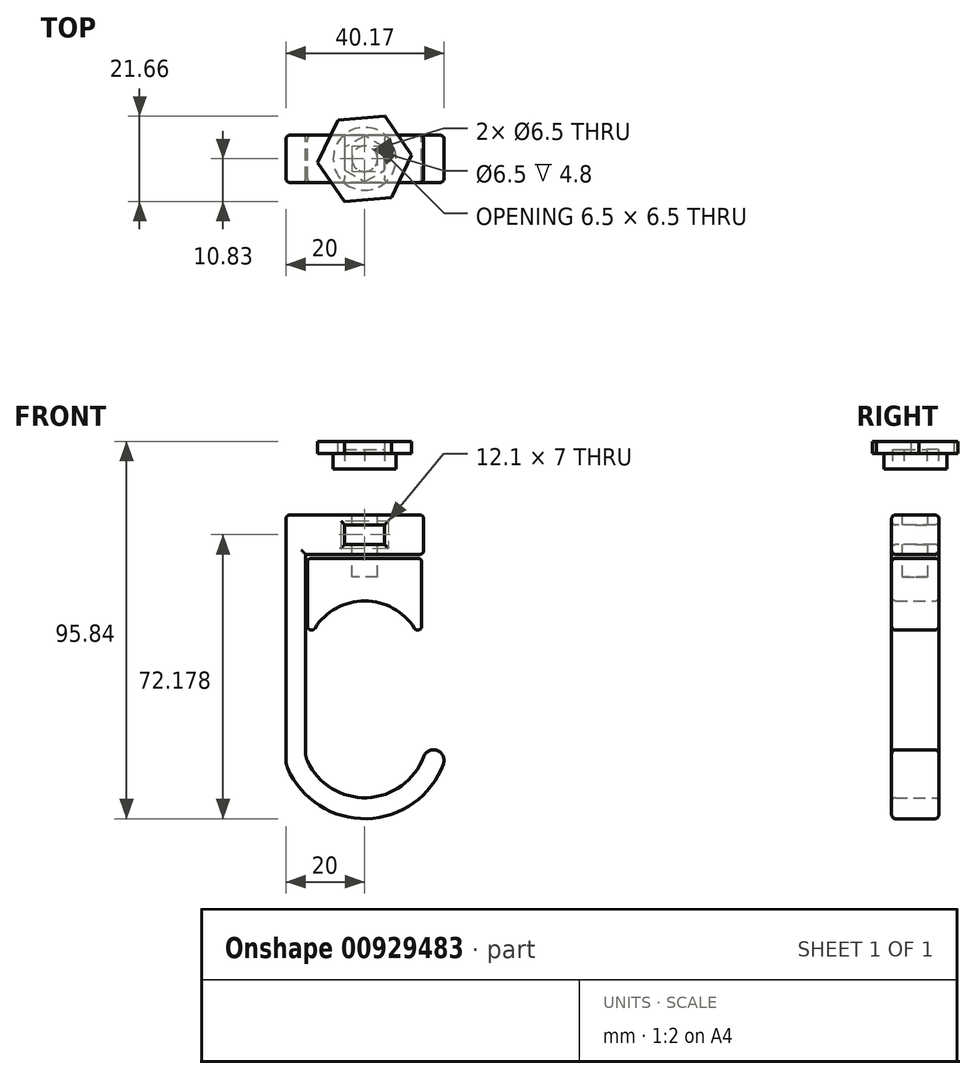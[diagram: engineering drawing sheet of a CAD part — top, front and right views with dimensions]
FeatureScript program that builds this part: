
annotation { "Feature Type Name" : "Feature", "Feature Type Description" : "" }
export const myFeature = defineFeature(function(context is Context, id is Id, definition is map)
    precondition{}
    {
        {
            var Q0;
            Q0=qCreatedBy(makeId("Front.planeOp"),FACE);
            var sketch = newSketch(context, id + "F0", { "sketchPlane" : qUnion([Q0])});
            skLineSegment(sketch, "E0", {"start": v(-15, 51.4) * mm, "end": v(-15, 0.99) * mm});
            skLineSegment(sketch, "E1", {"start": v(-15, 51.4) * mm, "end": v(15, 51.4) * mm});
            skLineSegment(sketch, "E2", {"start": v(15, 51.4) * mm, "end": v(15, 61.4) * mm});
            skLineSegment(sketch, "E3", {"start": v(15, 61.4) * mm, "end": v(-20, 61.4) * mm});
            skLineSegment(sketch, "E4", {"start": v(-20, 61.4) * mm, "end": v(-20, -0.9) * mm});
            skArc(sketch, "E5", {"start": v(20, -1.86) * mm, "mid": v(18.43, 1.57) * mm, "end": v(15, 0) * mm});
            skLineSegment(sketch, "E6", {"start": v(-14.5, 50.4) * mm, "end": v(14.5, 50.4) * mm});
            skLineSegment(sketch, "E7", {"start": v(14.5, 50.4) * mm, "end": v(14.5, 28.4) * mm});
            skLineSegment(sketch, "E8", {"start": v(-14.5, 50.4) * mm, "end": v(-14.5, 28.4) * mm});
            skPoint(sketch, "E9", {"position": v(0, 50.4) * mm});
            skArc(sketch, "E10", {"start": v(14.5, 28.4) * mm, "mid": v(0, 39.57) * mm, "end": v(-14.5, 28.4) * mm});
            skLineSegment(sketch, "E11", {"start": v(0, 80.07) * mm, "end": v(0, 73.07) * mm});
            skLineSegment(sketch, "E12", {"start": v(12, 77.07) * mm, "end": v(12, 80.07) * mm});
            skLineSegment(sketch, "E13", {"start": v(12, 80.07) * mm, "end": v(0, 80.07) * mm});
            skLineSegment(sketch, "E14", {"start": v(0, 73.07) * mm, "end": v(8, 73.07) * mm});
            skLineSegment(sketch, "E15", {"start": v(8, 73.07) * mm, "end": v(8, 77.07) * mm});
            skLineSegment(sketch, "E16", {"start": v(8, 77.07) * mm, "end": v(12, 77.07) * mm});
            skArc(sketch, "E17", {"start": v(-14.55, -1.1) * mm, "mid": v(0.6, -10.42) * mm, "end": v(15, 0) * mm});
            skArc(sketch, "E18", {"start": v(-19.6, -2.87) * mm, "mid": v(0.55, -15.76) * mm, "end": v(20, -1.86) * mm});
            skPoint(sketch, "E19.visualSharp", {"position": v(-20, -1.86) * mm});
            skArc(sketch, "E19.filletArc", {"start": v(-20, -0.9) * mm, "mid": v(-19.9, -1.9) * mm, "end": v(-19.6, -2.87) * mm});
            skLineSegment(sketch, "E20", {"start": v(-14.5, 42.07) * mm, "end": v(14.5, 42.07) * mm, "construction": true});
            skPoint(sketch, "E21.visualSharp", {"position": v(-15, 0) * mm});
            skArc(sketch, "E21.filletArc", {"start": v(-15, 0.99) * mm, "mid": v(-14.89, -0.08) * mm, "end": v(-14.55, -1.1) * mm});
            skSolve(sketch);
        }
        {
            var Q0;
            Q0=makeQuery(id+"F0.imprint","IMPRINT",FACE,{"disambiguationData":[TD([[makeQuery(id+"F0.imprint","IMPRINT",EDGE,{"derivedFrom":sQuery(id+"F0.wireOp",EDGE,"E0")}),-1.0]])]});
            var Q1;
            Q1=makeQuery(id+"F0.imprint","IMPRINT",FACE,{"disambiguationData":[TD([[makeQuery(id+"F0.imprint","IMPRINT",EDGE,{"derivedFrom":sQuery(id+"F0.wireOp",EDGE,"E6")}),-1.0]])]});
            extrude(context, id + "F1", {"entities" : qUnion([Q0, Q1]), "endBound" : BoundingType.SYMMETRIC, "depth" : 12 * mm, "offsetDistance" : 25 * mm});
        }
        {
            var Q0;
            Q0=makeQuery(id+"F0.imprint","IMPRINT",FACE,{"disambiguationData":[TD([[makeQuery(id+"F0.imprint","IMPRINT",EDGE,{"derivedFrom":sQuery(id+"F0.wireOp",EDGE,"E11")}),1.0]])]});
            var Q1;
            Q1=sQuery(id+"F0.wireOp",EDGE,"E11");
            revolve(context, id + "F2", {"surfaceOperationType" : NewSurfaceOperationType.NEW, "entities" : qUnion([Q0]), "axis" : qUnion([Q1]), "revolveType" : RevolveType.FULL});
        }
        {
            var Q0;
            Q0=makeQuery(id+"F1.opExtrude","SWEPT_FACE",FACE,{"disambiguationData":[OSD([sQuery(id+"F0.wireOp",EDGE,"E3")])]});
            var sketch = newSketch(context, id + "F3", { "sketchPlane" : qUnion([Q0])});
            skCircle(sketch, "E22", {"center": v(0, 0) * mm, "radius": 3.25 * mm});
            skSolve(sketch);
        }
        {
            var Q0;
            Q0=makeQuery(id+"F3.imprint","IMPRINT",FACE,{"disambiguationData":[TD([[makeQuery(id+"F3.imprint","IMPRINT",EDGE,{"derivedFrom":sQuery(id+"F3.wireOp",EDGE,"E22")}),1.0]])]});
            extrude(context, id + "F4", {"entities" : qUnion([Q0]), "operationType" : NewBodyOperationType.REMOVE, "surfaceOperationType" : NewSurfaceOperationType.ADD, "oppositeDirection" : true, "depth" : 15.8 * mm, "offsetDistance" : 25 * mm});
        }
        {
            var Q0;
            Q0=makeQuery(id+"F1.opExtrude","CAP_FACE",FACE,{"disambiguationData":[OSD([sQuery(id+"F0.wireOp",EDGE,"E0"),sQuery(id+"F0.wireOp",EDGE,"GksmTGkL-L8Wo-ihQQ-4q2p-oLHmUtR4vZST"),sQuery(id+"F0.wireOp",EDGE,"E1"),sQuery(id+"F0.wireOp",EDGE,"E2"),sQuery(id+"F0.wireOp",EDGE,"E3"),sQuery(id+"F0.wireOp",EDGE,"E4"),sQuery(id+"F0.wireOp",EDGE,"MIt5A5Y3-FBnd-N0LG-dI1h-DyVFCZma1lgl"),sQuery(id+"F0.wireOp",EDGE,"E5")])],"isStart":false});
            var sketch = newSketch(context, id + "F5", { "sketchPlane" : qUnion([Q0])});
            skLineSegment(sketch, "E23.bottom", {"start": v(-5.05, 58.9) * mm, "end": v(5.05, 58.9) * mm});
            skLineSegment(sketch, "E23.top", {"start": v(-5.05, 53.9) * mm, "end": v(5.05, 53.9) * mm});
            skLineSegment(sketch, "E23.left", {"start": v(-5.05, 58.9) * mm, "end": v(-5.05, 53.9) * mm});
            skLineSegment(sketch, "E23.right", {"start": v(5.05, 58.9) * mm, "end": v(5.05, 53.9) * mm});
            skPoint(sketch, "E24", {"position": v(-5.05, 56.4) * mm});
            skPoint(sketch, "E25", {"position": v(0, 58.9) * mm});
            skLineSegment(sketch, "E26", {"start": v(-9.97, 61.4) * mm, "end": v(-9.97, 51.4) * mm, "construction": true});
            skPoint(sketch, "E27", {"position": v(-9.97, 56.4) * mm});
            skSolve(sketch);
        }
        {
            var Q0;
            Q0=makeQuery(id+"F5.imprint","IMPRINT",FACE,{"disambiguationData":[TD([[makeQuery(id+"F5.imprint","IMPRINT",EDGE,{"derivedFrom":sQuery(id+"F5.wireOp",EDGE,"E23.bottom")}),-1.0]])]});
            extrude(context, id + "F6", {"entities" : qUnion([Q0]), "operationType" : NewBodyOperationType.REMOVE, "oppositeDirection" : true, "depth" : 25 * mm, "offsetDistance" : 25 * mm});
        }
        {
            var Q0;
            Q0=makeQuery(id+"F2.opRevolve","SWEPT_FACE",FACE,{"disambiguationData":[OSD([sQuery(id+"F0.wireOp",EDGE,"E14")])]});
            var sketch = newSketch(context, id + "F7", { "sketchPlane" : qUnion([Q0])});
            skCircle(sketch, "E28.cCircle", {"center": v(0, 0) * mm, "radius": 5.05 * mm, "construction": true});
            skLineSegment(sketch, "E28.0", {"start": v(5.05, 2.92) * mm, "end": v(5.05, -2.92) * mm});
            skLineSegment(sketch, "E28.1", {"start": v(5.05, -2.92) * mm, "end": v(0, -5.83) * mm});
            skLineSegment(sketch, "E28.2", {"start": v(0, -5.83) * mm, "end": v(-5.05, -2.92) * mm});
            skLineSegment(sketch, "E28.3", {"start": v(-5.05, -2.92) * mm, "end": v(-5.05, 2.92) * mm});
            skLineSegment(sketch, "E28.4", {"start": v(-5.05, 2.92) * mm, "end": v(0, 5.83) * mm});
            skLineSegment(sketch, "E28.5", {"start": v(0, 5.83) * mm, "end": v(5.05, 2.92) * mm});
            skPoint(sketch, "E28.0.midPoint", {"position": v(5.05, 0) * mm});
            skSolve(sketch);
        }
        {
            var Q0;
            Q0=makeQuery(id+"F7.imprint","IMPRINT",FACE,{"disambiguationData":[TD([[makeQuery(id+"F7.imprint","IMPRINT",EDGE,{"derivedFrom":sQuery(id+"F7.wireOp",EDGE,"E28.0")}),-1.0]])]});
            var Q1;
            Q1=makeQuery(id+"F2.opRevolve","SWEPT_FACE",FACE,{"disambiguationData":[OSD([sQuery(id+"F0.wireOp",EDGE,"E16")])]});
            extrude(context, id + "F8", {"entities" : qUnion([Q0]), "operationType" : NewBodyOperationType.REMOVE, "oppositeDirection" : true, "depth" : 5 * mm, "endBoundEntityFace" : qUnion([Q1]), "offsetDistance" : 25 * mm});
        }
        {
            var Q0;
            Q0=makeQuery(id+"F2.opRevolve","SWEPT_FACE",FACE,{"disambiguationData":[OSD([sQuery(id+"F0.wireOp",EDGE,"E13")])]});
            var sketch = newSketch(context, id + "F9", { "sketchPlane" : qUnion([Q0])});
            skCircle(sketch, "E29.cCircle", {"center": v(0, 0) * mm, "radius": 10.4 * mm, "construction": true});
            skLineSegment(sketch, "E29.0", {"start": v(5.16, 10.83) * mm, "end": v(11.96, 0.95) * mm});
            skLineSegment(sketch, "E29.1", {"start": v(11.96, 0.95) * mm, "end": v(6.8, -9.89) * mm});
            skLineSegment(sketch, "E29.2", {"start": v(6.8, -9.89) * mm, "end": v(-5.16, -10.83) * mm});
            skLineSegment(sketch, "E29.3", {"start": v(-5.16, -10.83) * mm, "end": v(-11.96, -0.95) * mm});
            skLineSegment(sketch, "E29.4", {"start": v(-11.96, -0.95) * mm, "end": v(-6.8, 9.89) * mm});
            skLineSegment(sketch, "E29.5", {"start": v(-6.8, 9.89) * mm, "end": v(5.16, 10.83) * mm});
            skPoint(sketch, "E29.0.midPoint", {"position": v(8.56, 5.89) * mm});
            skSolve(sketch);
        }
        {
            var Q0;
            Q0=makeQuery(id+"F9.imprint","IMPRINT",FACE,{"disambiguationData":[TD([[makeQuery(id+"F9.imprint","IMPRINT",EDGE,{"derivedFrom":sQuery(id+"F9.wireOp",EDGE,"E29.0")}),-1.0]])]});
            extrude(context, id + "F10", {"entities" : qUnion([Q0]), "oppositeDirection" : true, "depth" : 12 * mm, "offsetDistance" : 25 * mm});
        }
        {
            var Q0;
            Q0=makeQuery(id+"F2.opRevolve","SWEPT_BODY",BODY,{"disambiguationData":[OSD([sQuery(id+"F0.wireOp",EDGE,"E11"),sQuery(id+"F0.wireOp",EDGE,"E12"),sQuery(id+"F0.wireOp",EDGE,"E13"),sQuery(id+"F0.wireOp",EDGE,"E14"),sQuery(id+"F0.wireOp",EDGE,"E15"),sQuery(id+"F0.wireOp",EDGE,"E16")])]});
            var Q1;
            Q1=makeQuery(id+"F10.opExtrude","SWEPT_BODY",BODY,{"disambiguationData":[OSD([sQuery(id+"F9.wireOp",EDGE,"E29.0"),sQuery(id+"F9.wireOp",EDGE,"E29.1"),sQuery(id+"F9.wireOp",EDGE,"E29.2"),sQuery(id+"F9.wireOp",EDGE,"E29.3"),sQuery(id+"F9.wireOp",EDGE,"E29.4"),sQuery(id+"F9.wireOp",EDGE,"E29.5")])]});
            booleanBodies(context, id + "F11", {"operationType" : BooleanOperationType.INTERSECTION, "tools" : qUnion([Q0, Q1])});
        }
        {
            var Q0;
            Q0=makeQuery(id+"F1.opExtrude","CAP_FACE",FACE,{"disambiguationData":[OSD([sQuery(id+"F0.wireOp",EDGE,"E0"),sQuery(id+"F0.wireOp",EDGE,"GksmTGkL-L8Wo-ihQQ-4q2p-oLHmUtR4vZST"),sQuery(id+"F0.wireOp",EDGE,"E1"),sQuery(id+"F0.wireOp",EDGE,"E2"),sQuery(id+"F0.wireOp",EDGE,"E3"),sQuery(id+"F0.wireOp",EDGE,"E4"),sQuery(id+"F0.wireOp",EDGE,"MIt5A5Y3-FBnd-N0LG-dI1h-DyVFCZma1lgl"),sQuery(id+"F0.wireOp",EDGE,"E5")])],"isStart":false});
            var Q1;
            Q1=makeQuery(id+"F1.opExtrude","CAP_FACE",FACE,{"disambiguationData":[OSD([sQuery(id+"F0.wireOp",EDGE,"E0"),sQuery(id+"F0.wireOp",EDGE,"GksmTGkL-L8Wo-ihQQ-4q2p-oLHmUtR4vZST"),sQuery(id+"F0.wireOp",EDGE,"E1"),sQuery(id+"F0.wireOp",EDGE,"E2"),sQuery(id+"F0.wireOp",EDGE,"E3"),sQuery(id+"F0.wireOp",EDGE,"E4"),sQuery(id+"F0.wireOp",EDGE,"MIt5A5Y3-FBnd-N0LG-dI1h-DyVFCZma1lgl"),sQuery(id+"F0.wireOp",EDGE,"E5")])],"isStart":true});
            var Q2;
            Q2=makeQuery(id+"F1.opExtrude","SWEPT_FACE",FACE,{"disambiguationData":[OSD([sQuery(id+"F0.wireOp",EDGE,"E2")])]});
            var Q3;
            Q3=makeQuery(id+"F1.opExtrude","SWEPT_FACE",FACE,{"disambiguationData":[OSD([sQuery(id+"F0.wireOp",EDGE,"E4")])]});
            var Q4;
            Q4=makeQuery(id+"F1.opExtrude","CAP_FACE",FACE,{"disambiguationData":[OSD([sQuery(id+"F0.wireOp",EDGE,"E6"),sQuery(id+"F0.wireOp",EDGE,"E7"),sQuery(id+"F0.wireOp",EDGE,"E8"),sQuery(id+"F0.wireOp",EDGE,"E10")])],"isStart":false});
            var Q5;
            Q5=makeQuery(id+"F1.opExtrude","CAP_FACE",FACE,{"disambiguationData":[OSD([sQuery(id+"F0.wireOp",EDGE,"E6"),sQuery(id+"F0.wireOp",EDGE,"E7"),sQuery(id+"F0.wireOp",EDGE,"E8"),sQuery(id+"F0.wireOp",EDGE,"E10")])],"isStart":true});
            var Q6;
            Q6=makeQuery(id+"F1.opExtrude","SWEPT_FACE",FACE,{"disambiguationData":[OSD([sQuery(id+"F0.wireOp",EDGE,"E7")])]});
            var Q7;
            Q7=makeQuery(id+"F1.opExtrude","SWEPT_FACE",FACE,{"disambiguationData":[OSD([sQuery(id+"F0.wireOp",EDGE,"E8")])]});
            fillet(context, id + "F12", {"entities" : qUnion([Q0, Q1, Q2, Q3, Q4, Q5, Q6, Q7]), "radius" : 1 * mm, "tangentPropagation" : true, "allowEdgeOverflow" : false});
        }
    });
